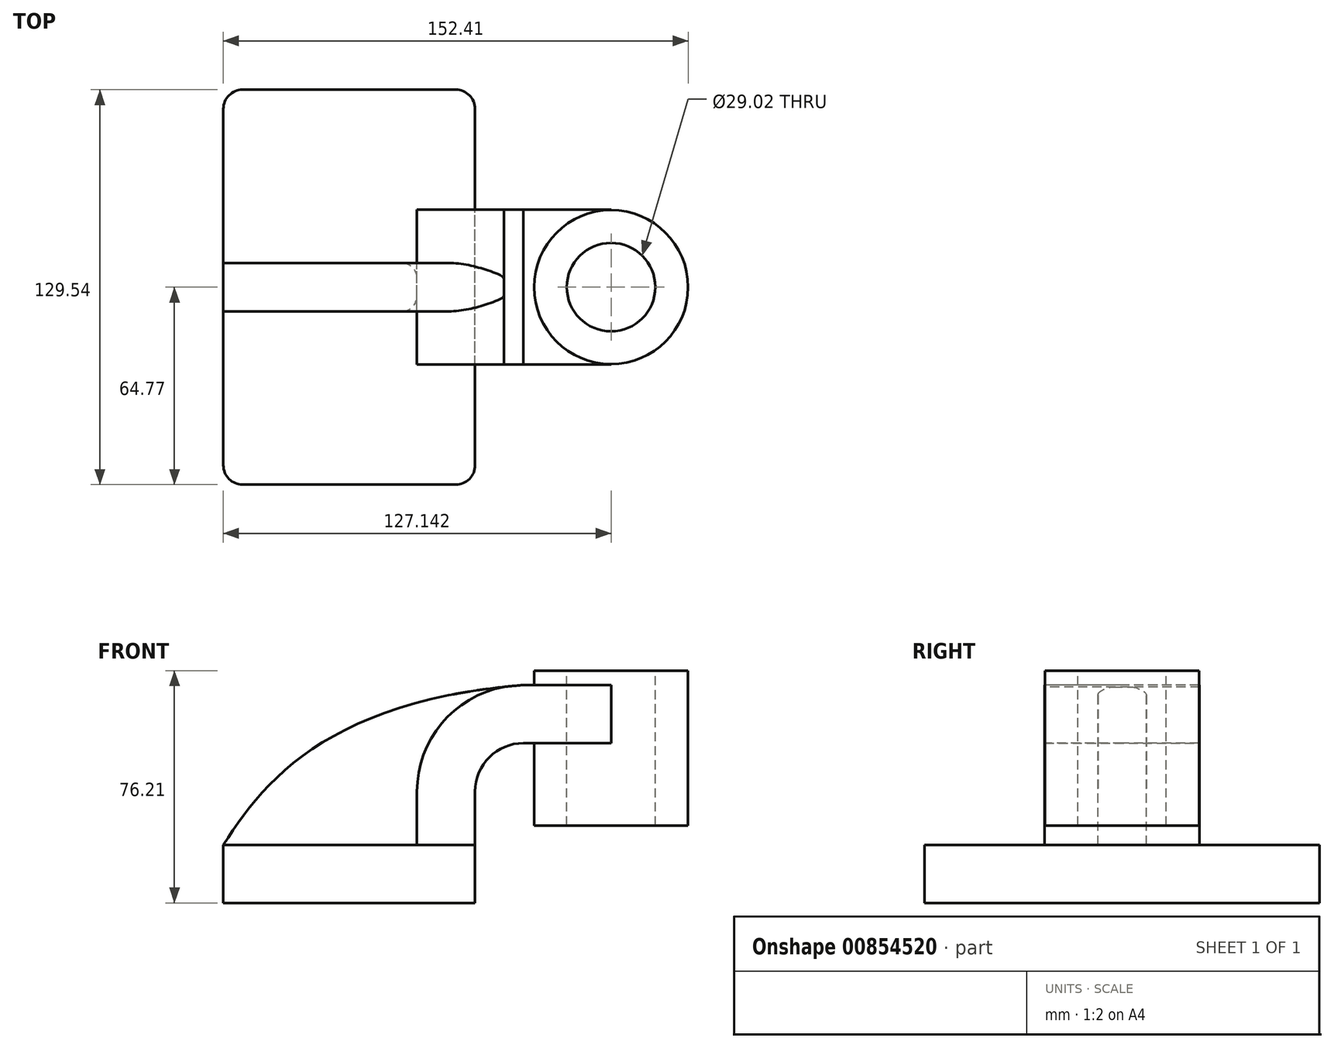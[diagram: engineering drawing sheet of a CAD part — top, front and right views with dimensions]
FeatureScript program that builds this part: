
annotation { "Feature Type Name" : "Feature", "Feature Type Description" : "" }
export const myFeature = defineFeature(function(context is Context, id is Id, definition is map)
    precondition{}
    {
        {
            var Q0;
            Q0=qCreatedBy(makeId("Front.planeOp"),FACE);
            var sketch = newSketch(context, id + "F0", { "sketchPlane" : qUnion([Q0])});
            skLineSegment(sketch, "E0.bottom", {"start": v(41.28, -9.52) * mm, "end": v(-41.27, -9.53) * mm});
            skLineSegment(sketch, "E0.top", {"start": v(41.27, 9.53) * mm, "end": v(-41.28, 9.52) * mm});
            skLineSegment(sketch, "E0.left", {"start": v(41.27, -9.53) * mm, "end": v(41.27, 9.53) * mm});
            skLineSegment(sketch, "E0.right", {"start": v(-41.27, -9.53) * mm, "end": v(-41.28, 9.52) * mm});
            skPoint(sketch, "E0.middle", {"position": v(0, 0) * mm});
            skLineSegment(sketch, "E1", {"start": v(41.27, 9.53) * mm, "end": v(41.27, 27) * mm});
            skArc(sketch, "E2", {"start": v(41.27, 27) * mm, "mid": v(45.92, 38.23) * mm, "end": v(57.15, 42.88) * mm});
            skLineSegment(sketch, "E3", {"start": v(57.15, 42.88) * mm, "end": v(85.86, 42.88) * mm});
            skLineSegment(sketch, "E4.bottom", {"start": v(111.12, 15.88) * mm, "end": v(60.32, 15.88) * mm});
            skLineSegment(sketch, "E4.top", {"start": v(111.13, 66.68) * mm, "end": v(60.33, 66.68) * mm});
            skLineSegment(sketch, "E4.left", {"start": v(111.12, 15.88) * mm, "end": v(111.12, 66.68) * mm});
            skLineSegment(sketch, "E4.right", {"start": v(60.32, 15.88) * mm, "end": v(60.32, 66.68) * mm});
            skPoint(sketch, "E4.middle", {"position": v(85.72, 41.28) * mm});
            skLineSegment(sketch, "E5.0", {"start": v(57.15, 61.93) * mm, "end": v(85.86, 61.93) * mm});
            skArc(sketch, "E5.1", {"start": v(22.22, 27) * mm, "mid": v(32.45, 51.7) * mm, "end": v(57.15, 61.93) * mm});
            skLineSegment(sketch, "E5.2", {"start": v(22.22, 9.53) * mm, "end": v(22.22, 27) * mm});
            skLineSegment(sketch, "E6", {"start": v(85.86, 15.88) * mm, "end": v(85.86, 66.68) * mm});
            skFitSpline(sketch, "E7", {"points": [v(-41.28, 9.52) * mm, v(57.15, 61.93) * mm], "startDerivative": vector(40.1, 63.72) * mm, "endDerivative": vector(190.15, 15.17) * mm});
            skSolve(sketch);
        }
        {
            var Q0;
            Q0=makeQuery(id+"F0.imprint","IMPRINT",FACE,{"disambiguationData":[TD([[makeQuery(id+"F0.imprint","IMPRINT",EDGE,{"derivedFrom":sQuery(id+"F0.wireOp",EDGE,"E0.bottom")}),-1.0]])]});
            extrude(context, id + "F1", {"entities" : qUnion([Q0]), "endBound" : BoundingType.SYMMETRIC, "depth" : 129.54 * mm, "offsetDistance" : 25.4 * mm});
        }
        {
            var Q0;
            {var subQ4=sQuery(id+"F0.wireOp",EDGE,"E1");Q0=makeQuery(id+"F0.imprint","IMPRINT",FACE,{"disambiguationData":[TD([[makeQuery(id+"F0.imprint","IMPRINT",EDGE,{"derivedFrom":subQ4}),1.0]])]});}
            var Q1;
            {var subQ0=sQuery(id+"F0.wireOp",EDGE,"E6");var subQ1=sQuery(id+"F0.wireOp",EDGE,"E3");var subQ2=makeQuery(id+"F0.imprint","INTERSECT",VERTEX,{"derivedFrom":[subQ1,subQ0]});Q1=makeQuery(id+"F0.imprint","IMPRINT",FACE,{"disambiguationData":[TD([[makeQuery(id+"F0.imprint","IMPRINT",EDGE,{"disambiguationData":[TD([[subQ2,1.0]])],"derivedFrom":subQ1}),1.0]])]});}
            extrude(context, id + "F2", {"entities" : qUnion([Q0, Q1]), "endBound" : BoundingType.SYMMETRIC, "depth" : 50.8 * mm, "offsetDistance" : 25.4 * mm});
        }
        {
            var Q0;
            {var subQ3=sQuery(id+"F0.wireOp",EDGE,"E5.2");Q0=makeQuery(id+"F0.imprint","IMPRINT",FACE,{"disambiguationData":[TD([[makeQuery(id+"F0.imprint","IMPRINT",EDGE,{"derivedFrom":subQ3}),1.0]])]});}
            extrude(context, id + "F3", {"entities" : qUnion([Q0]), "endBound" : BoundingType.SYMMETRIC, "depth" : 15.88 * mm, "offsetDistance" : 25.4 * mm});
        }
        {
            var Q0;
            {var subQ4=sQuery(id+"F0.wireOp",EDGE,"E4.left");Q0=makeQuery(id+"F0.imprint","IMPRINT",FACE,{"disambiguationData":[TD([[makeQuery(id+"F0.imprint","IMPRINT",EDGE,{"derivedFrom":subQ4}),1.0]])]});}
            var Q1;
            Q1=sQuery(id+"F0.wireOp",EDGE,"E6");
            revolve(context, id + "F4", {"operationType" : NewBodyOperationType.ADD, "surfaceOperationType" : NewSurfaceOperationType.NEW, "entities" : qUnion([Q0]), "axis" : qUnion([Q1]), "revolveType" : RevolveType.FULL});
        }
        {
            var Q0;
            Q0=makeQuery(id+"F1.opExtrude","CAP_EDGE",EDGE,{"disambiguationData":[OSD([sQuery(id+"F0.wireOp",EDGE,"E0.right")])],"isStart":true});
            var Q1;
            Q1=makeQuery(id+"F1.opExtrude","CAP_EDGE",EDGE,{"disambiguationData":[OSD([sQuery(id+"F0.wireOp",EDGE,"E0.left")])],"isStart":true});
            var Q2;
            Q2=makeQuery(id+"F1.opExtrude","CAP_EDGE",EDGE,{"disambiguationData":[OSD([sQuery(id+"F0.wireOp",EDGE,"E0.right")])],"isStart":false});
            var Q3;
            Q3=makeQuery(id+"F1.opExtrude","CAP_EDGE",EDGE,{"disambiguationData":[OSD([sQuery(id+"F0.wireOp",EDGE,"E0.left")])],"isStart":false});
            fillet(context, id + "F5", {"entities" : qUnion([Q0, Q1, Q2, Q3]), "radius" : 6.35 * mm, "tangentPropagation" : true, "allowEdgeOverflow" : false});
        }
        {
            var Q0;
            Q0=makeQuery(id+"F3.opExtrude","CAP_EDGE",EDGE,{"disambiguationData":[OSD([sQuery(id+"F0.wireOp",EDGE,"E5.1")])],"isStart":true});
            var Q1;
            Q1=makeQuery(id+"F3.opExtrude","CAP_EDGE",EDGE,{"disambiguationData":[OSD([sQuery(id+"F0.wireOp",EDGE,"E5.2")])],"isStart":true});
            var Q2;
            Q2=makeQuery(id+"F3.opExtrude","CAP_EDGE",EDGE,{"disambiguationData":[OSD([sQuery(id+"F0.wireOp",EDGE,"E5.1")])],"isStart":false});
            fillet(context, id + "F6", {"entities" : qUnion([Q0, Q1, Q2]), "radius" : 5.08 * mm, "tangentPropagation" : true, "allowEdgeOverflow" : false});
        }
        {
            var Q0;
            Q0=makeQuery(id+"F4.opRevolve","SWEPT_FACE",FACE,{"disambiguationData":[OSD([sQuery(id+"F0.wireOp",EDGE,"E4.top")])]});
            var sketch = newSketch(context, id + "F7", { "sketchPlane" : qUnion([Q0])});
            skCircle(sketch, "E8", {"center": v(85.86, 0) * mm, "radius": 14.5 * mm});
            skSolve(sketch);
        }
        {
            var Q0;
            Q0=makeQuery(id+"F7.imprint","IMPRINT",FACE,{"disambiguationData":[TD([[makeQuery(id+"F7.imprint","IMPRINT",EDGE,{"derivedFrom":sQuery(id+"F7.wireOp",EDGE,"E8")}),1.0]])]});
            var Q1;
            Q1=makeQuery(id+"F4.opRevolve","SWEPT_FACE",FACE,{"disambiguationData":[OSD([sQuery(id+"F0.wireOp",EDGE,"E4.bottom")])]});
            extrude(context, id + "F8", {"entities" : qUnion([Q0]), "operationType" : NewBodyOperationType.REMOVE, "endBound" : BoundingType.THROUGH_ALL, "oppositeDirection" : true, "depth" : 95.5 * mm, "endBoundEntityFace" : qUnion([Q1]), "offsetDistance" : 25.4 * mm});
        }
    });
